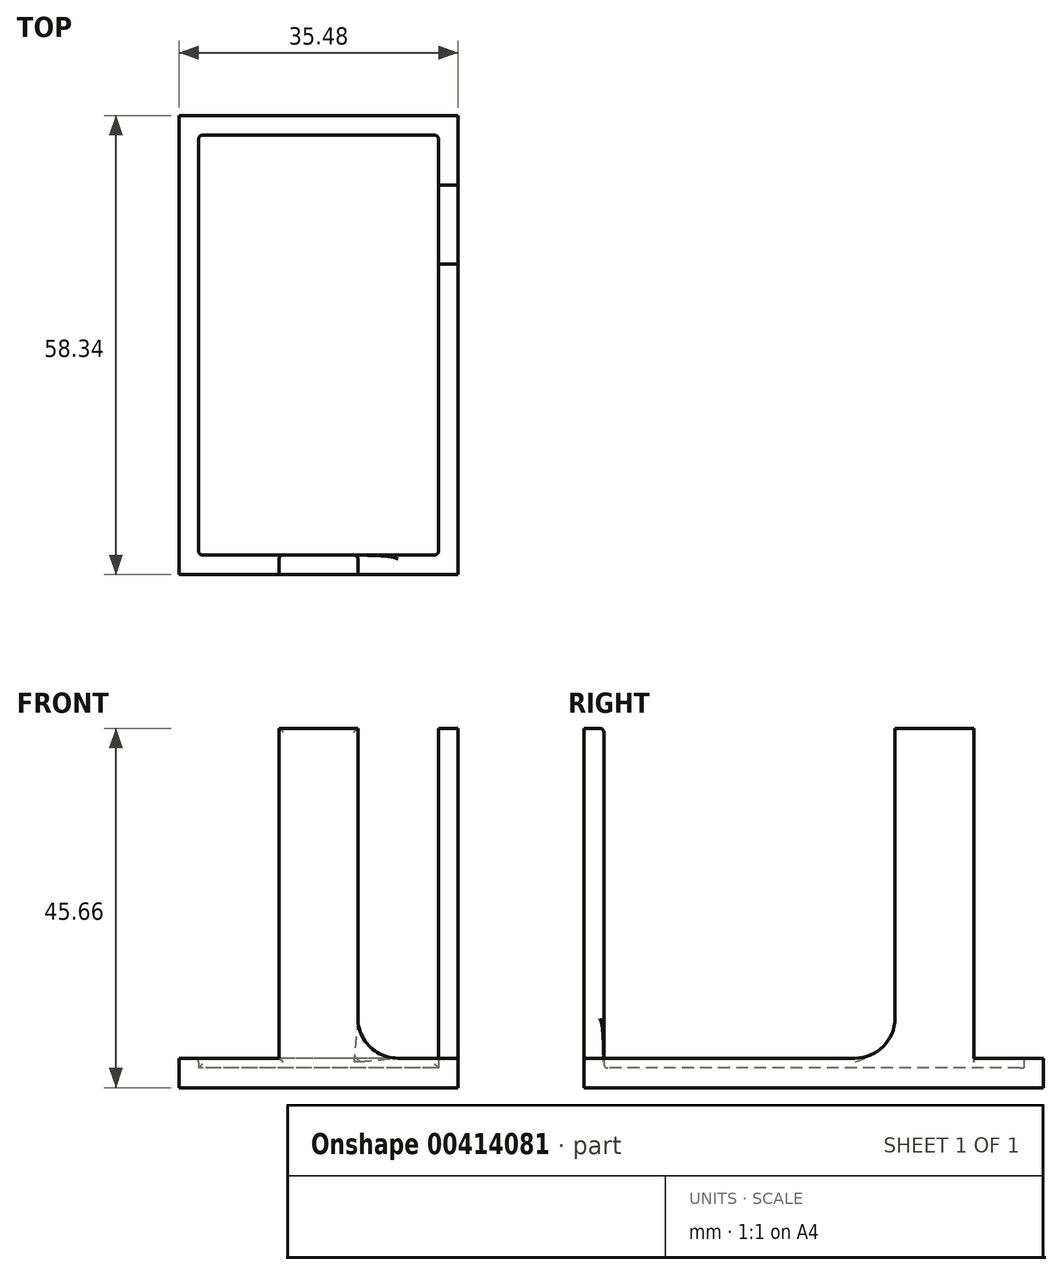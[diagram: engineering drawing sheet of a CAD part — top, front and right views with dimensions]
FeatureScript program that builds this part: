
annotation { "Feature Type Name" : "Feature", "Feature Type Description" : "" }
export const myFeature = defineFeature(function(context is Context, id is Id, definition is map)
    precondition{}
    {
        {
            var Q0;
            Q0=qCreatedBy(makeId("Top.planeOp"),FACE);
            var sketch = newSketch(context, id + "F0", { "sketchPlane" : qUnion([Q0])});
            skLineSegment(sketch, "E0.bottom", {"start": v(15.24, 26.67) * mm, "end": v(-15.24, 26.67) * mm});
            skLineSegment(sketch, "E0.top", {"start": v(15.24, -26.67) * mm, "end": v(-15.24, -26.67) * mm});
            skLineSegment(sketch, "E0.left", {"start": v(15.24, 26.67) * mm, "end": v(15.24, -26.67) * mm});
            skLineSegment(sketch, "E0.right", {"start": v(-15.24, 26.67) * mm, "end": v(-15.24, -26.67) * mm});
            skPoint(sketch, "E0.middle", {"position": v(0, 0) * mm});
            skSolve(sketch);
        }
        {
            var Q0;
            Q0=makeQuery(id+"F0.imprint","IMPRINT",FACE,{"disambiguationData":[TD([[makeQuery(id+"F0.imprint","IMPRINT",EDGE,{"derivedFrom":sQuery(id+"F0.wireOp",EDGE,"E0.bottom")}),1.0]])]});
            extrude(context, id + "F1", {"entities" : qUnion([Q0]), "depth" : 2.5 * mm});
        }
        {
            var Q0;
            Q0=makeQuery(id+"F1.opExtrude","SWEPT_FACE",FACE,{"disambiguationData":[OSD([sQuery(id+"F0.wireOp",EDGE,"E0.left")])]});
            var sketch = newSketch(context, id + "F2", { "sketchPlane" : qUnion([Q0])});
            skLineSegment(sketch, "E1.bottom", {"start": v(-26.67, 0) * mm, "end": v(26.67, 0) * mm});
            skLineSegment(sketch, "E1.top", {"start": v(-26.67, 1.25) * mm, "end": v(26.67, 1.25) * mm});
            skLineSegment(sketch, "E1.left", {"start": v(-26.67, 0) * mm, "end": v(-26.67, 1.25) * mm});
            skLineSegment(sketch, "E1.right", {"start": v(26.67, 0) * mm, "end": v(26.67, 1.25) * mm});
            skSolve(sketch);
        }
        {
            var Q0;
            Q0=makeQuery(id+"F1.opExtrude","SWEPT_FACE",FACE,{"disambiguationData":[OSD([sQuery(id+"F0.wireOp",EDGE,"E0.bottom")])]});
            var sketch = newSketch(context, id + "F3", { "sketchPlane" : qUnion([Q0])});
            skLineSegment(sketch, "E2.bottom", {"start": v(-15.24, 0) * mm, "end": v(15.24, 0) * mm});
            skLineSegment(sketch, "E2.top", {"start": v(-15.24, 1.25) * mm, "end": v(15.24, 1.25) * mm});
            skLineSegment(sketch, "E2.left", {"start": v(-15.24, 0) * mm, "end": v(-15.24, 1.25) * mm});
            skLineSegment(sketch, "E2.right", {"start": v(15.24, 0) * mm, "end": v(15.24, 1.25) * mm});
            skSolve(sketch);
        }
        {
            var Q0;
            Q0=makeQuery(id+"F1.opExtrude","SWEPT_FACE",FACE,{"disambiguationData":[OSD([sQuery(id+"F0.wireOp",EDGE,"E0.right")])]});
            var sketch = newSketch(context, id + "F4", { "sketchPlane" : qUnion([Q0])});
            skLineSegment(sketch, "E3.bottom", {"start": v(-26.67, 0) * mm, "end": v(26.67, 0) * mm});
            skLineSegment(sketch, "E3.top", {"start": v(-26.67, 1.25) * mm, "end": v(26.67, 1.25) * mm});
            skLineSegment(sketch, "E3.left", {"start": v(-26.67, 0) * mm, "end": v(-26.67, 1.25) * mm});
            skLineSegment(sketch, "E3.right", {"start": v(26.67, 0) * mm, "end": v(26.67, 1.25) * mm});
            skSolve(sketch);
        }
        {
            var Q0;
            Q0=makeQuery(id+"F1.opExtrude","SWEPT_FACE",FACE,{"disambiguationData":[OSD([sQuery(id+"F0.wireOp",EDGE,"E0.top")])]});
            var sketch = newSketch(context, id + "F5", { "sketchPlane" : qUnion([Q0])});
            skLineSegment(sketch, "E4.bottom", {"start": v(-15.24, 0) * mm, "end": v(15.24, 0) * mm});
            skLineSegment(sketch, "E4.top", {"start": v(-15.24, 1.25) * mm, "end": v(15.24, 1.25) * mm});
            skLineSegment(sketch, "E4.left", {"start": v(-15.24, 0) * mm, "end": v(-15.24, 1.25) * mm});
            skLineSegment(sketch, "E4.right", {"start": v(15.24, 0) * mm, "end": v(15.24, 1.25) * mm});
            skSolve(sketch);
        }
        {
            var Q0;
            Q0=makeQuery(id+"F2.imprint","IMPRINT",FACE,{"disambiguationData":[TD([[makeQuery(id+"F2.imprint","IMPRINT",EDGE,{"derivedFrom":sQuery(id+"F2.wireOp",EDGE,"E1.bottom")}),-1.0]])]});
            extrude(context, id + "F6", {"entities" : qUnion([Q0]), "operationType" : NewBodyOperationType.ADD, "depth" : 2.5 * mm});
        }
        {
            var Q0;
            Q0=makeQuery(id+"F5.imprint","IMPRINT",FACE,{"disambiguationData":[TD([[makeQuery(id+"F5.imprint","IMPRINT",EDGE,{"derivedFrom":sQuery(id+"F5.wireOp",EDGE,"E4.bottom")}),-1.0]])]});
            extrude(context, id + "F7", {"entities" : qUnion([Q0]), "operationType" : NewBodyOperationType.ADD, "depth" : 2.5 * mm});
        }
        {
            var Q0;
            Q0=makeQuery(id+"F7.opExtrude","SWEPT_FACE",FACE,{"disambiguationData":[OSD([sQuery(id+"F5.wireOp",EDGE,"E4.right")])]});
            extrude(context, id + "F8", {"entities" : qUnion([Q0]), "operationType" : NewBodyOperationType.ADD, "depth" : 2.5 * mm});
        }
        {
            var Q0;
            Q0=makeQuery(id+"F4.imprint","IMPRINT",FACE,{"disambiguationData":[TD([[makeQuery(id+"F4.imprint","IMPRINT",EDGE,{"derivedFrom":sQuery(id+"F4.wireOp",EDGE,"E3.bottom")}),1.0]])]});
            extrude(context, id + "F9", {"entities" : qUnion([Q0]), "operationType" : NewBodyOperationType.ADD, "depth" : 2.5 * mm});
        }
        {
            var Q0;
            Q0=makeQuery(id+"F9.opExtrude","SWEPT_FACE",FACE,{"disambiguationData":[OSD([sQuery(id+"F4.wireOp",EDGE,"E3.right")])]});
            extrude(context, id + "F10", {"entities" : qUnion([Q0]), "operationType" : NewBodyOperationType.ADD, "depth" : 2.5 * mm});
        }
        {
            var Q0;
            Q0=makeQuery(id+"F3.imprint","IMPRINT",FACE,{"disambiguationData":[TD([[makeQuery(id+"F3.imprint","IMPRINT",EDGE,{"derivedFrom":sQuery(id+"F3.wireOp",EDGE,"E2.bottom")}),1.0]])]});
            extrude(context, id + "F11", {"entities" : qUnion([Q0]), "operationType" : NewBodyOperationType.ADD, "depth" : 2.5 * mm});
        }
        {
            var Q0;
            Q0=makeQuery(id+"F11.opExtrude","SWEPT_FACE",FACE,{"disambiguationData":[OSD([sQuery(id+"F3.wireOp",EDGE,"E2.left")])]});
            extrude(context, id + "F12", {"entities" : qUnion([Q0]), "operationType" : NewBodyOperationType.ADD, "depth" : 2.5 * mm});
        }
        {
            var Q0;
            Q0=makeQuery(id+"F11.opExtrude","SWEPT_FACE",FACE,{"disambiguationData":[OSD([sQuery(id+"F3.wireOp",EDGE,"E2.right")])]});
            extrude(context, id + "F13", {"entities" : qUnion([Q0]), "operationType" : NewBodyOperationType.ADD, "depth" : 2.5 * mm});
        }
        {
            var Q0;
            {var subQ0=sQuery(id+"F3.wireOp",EDGE,"E2.top");var subQ1=sQuery(id+"F0.wireOp",EDGE,"E0.right");var subQ2=sQuery(id+"F0.wireOp",EDGE,"E0.bottom");var subQ3=sQuery(id+"F0.wireOp",EDGE,"E0.left");var subQ4=sQuery(id+"F4.wireOp",EDGE,"E3.top");var subQ5=sQuery(id+"F0.wireOp",EDGE,"E0.top");var subQ6=sQuery(id+"F5.wireOp",EDGE,"E4.top");Q0=makeQuery(id+"F13.boolean.opBoolean","MERGE",FACE,{"derivedFrom":[makeQuery(id+"F12.boolean.opBoolean","MERGE",FACE,{"derivedFrom":[makeQuery(id+"F10.boolean.opBoolean","MERGE",FACE,{"derivedFrom":[makeQuery(id+"F8.boolean.opBoolean","MERGE",FACE,{"derivedFrom":[makeQuery(id+"F6.opExtrude","SWEPT_FACE",FACE,{"disambiguationData":[OSD([sQuery(id+"F2.wireOp",EDGE,"E1.top")])]}),makeQuery(id+"F7.opExtrude","SWEPT_FACE",FACE,{"disambiguationData":[OSD([subQ6])]}),makeQuery(id+"F8.opExtrude","SWEPT_FACE",FACE,{"disambiguationData":[OSD([subQ5,subQ3,subQ6,sQuery(id+"F5.wireOp",EDGE,"E4.right")])]})]}),makeQuery(id+"F9.opExtrude","SWEPT_FACE",FACE,{"disambiguationData":[OSD([subQ4])]}),makeQuery(id+"F10.opExtrude","SWEPT_FACE",FACE,{"disambiguationData":[OSD([subQ5,subQ1,subQ4,sQuery(id+"F4.wireOp",EDGE,"E3.right")])]})]}),makeQuery(id+"F11.opExtrude","SWEPT_FACE",FACE,{"disambiguationData":[OSD([subQ0])]}),makeQuery(id+"F12.opExtrude","SWEPT_FACE",FACE,{"disambiguationData":[OSD([subQ2,subQ3,subQ0,sQuery(id+"F3.wireOp",EDGE,"E2.left")])]})]}),makeQuery(id+"F13.opExtrude","SWEPT_FACE",FACE,{"disambiguationData":[OSD([subQ2,subQ1,subQ0,sQuery(id+"F3.wireOp",EDGE,"E2.right")])]})]});}
            extrude(context, id + "F14", {"entities" : qUnion([Q0]), "operationType" : NewBodyOperationType.ADD, "depth" : 2.5 * mm});
        }
        {
            var Q0;
            Q0=makeQuery(id+"F14.opExtrude","CAP_FACE",FACE,{"disambiguationData":[OSD([sQuery(id+"F0.wireOp",EDGE,"E0.bottom"),sQuery(id+"F0.wireOp",EDGE,"E0.top"),sQuery(id+"F0.wireOp",EDGE,"E0.left"),sQuery(id+"F0.wireOp",EDGE,"E0.right"),sQuery(id+"F2.wireOp",EDGE,"E1.top"),sQuery(id+"F3.wireOp",EDGE,"E2.top"),sQuery(id+"F3.wireOp",EDGE,"E2.left"),sQuery(id+"F3.wireOp",EDGE,"E2.right"),sQuery(id+"F4.wireOp",EDGE,"E3.top"),sQuery(id+"F4.wireOp",EDGE,"E3.right"),sQuery(id+"F5.wireOp",EDGE,"E4.top"),sQuery(id+"F5.wireOp",EDGE,"E4.right")])],"isStart":false});
            var sketch = newSketch(context, id + "F15", { "sketchPlane" : qUnion([Q0])});
            skLineSegment(sketch, "E5.top", {"start": v(-15.24, -20.32) * mm, "end": v(-17.74, -20.32) * mm});
            skLineSegment(sketch, "E5.left", {"start": v(-15.24, -26.67) * mm, "end": v(-15.24, -20.32) * mm});
            skLineSegment(sketch, "E5.right", {"start": v(-17.74, -26.67) * mm, "end": v(-17.74, -20.32) * mm});
            skLineSegment(sketch, "E6.bottom", {"start": v(-17.74, -20.32) * mm, "end": v(-15.24, -20.32) * mm});
            skLineSegment(sketch, "E6.top", {"start": v(-17.74, -10.32) * mm, "end": v(-15.24, -10.32) * mm});
            skLineSegment(sketch, "E6.left", {"start": v(-17.74, -20.32) * mm, "end": v(-17.74, -10.32) * mm});
            skLineSegment(sketch, "E6.right", {"start": v(-15.24, -20.32) * mm, "end": v(-15.24, -10.32) * mm});
            skLineSegment(sketch, "E7.top", {"start": v(-15.24, 20.32) * mm, "end": v(-17.74, 20.32) * mm});
            skLineSegment(sketch, "E7.left", {"start": v(-15.24, 26.67) * mm, "end": v(-15.24, 20.32) * mm});
            skLineSegment(sketch, "E7.right", {"start": v(-17.74, 26.67) * mm, "end": v(-17.74, 20.32) * mm});
            skLineSegment(sketch, "E8.bottom", {"start": v(-17.74, 20.32) * mm, "end": v(-15.24, 20.32) * mm});
            skLineSegment(sketch, "E8.top", {"start": v(-17.74, 10.32) * mm, "end": v(-15.24, 10.32) * mm});
            skLineSegment(sketch, "E8.left", {"start": v(-17.74, 20.32) * mm, "end": v(-17.74, 10.32) * mm});
            skLineSegment(sketch, "E8.right", {"start": v(-15.24, 20.32) * mm, "end": v(-15.24, 10.32) * mm});
            skLineSegment(sketch, "E9.top", {"start": v(15.24, 20.32) * mm, "end": v(17.74, 20.32) * mm});
            skLineSegment(sketch, "E9.left", {"start": v(15.24, 26.67) * mm, "end": v(15.24, 20.32) * mm});
            skLineSegment(sketch, "E9.right", {"start": v(17.74, 26.67) * mm, "end": v(17.74, 20.32) * mm});
            skLineSegment(sketch, "E10.bottom", {"start": v(15.24, 10.32) * mm, "end": v(17.74, 10.32) * mm});
            skLineSegment(sketch, "E10.left", {"start": v(15.24, 10.32) * mm, "end": v(15.24, 20.32) * mm});
            skLineSegment(sketch, "E10.right", {"start": v(17.74, 10.32) * mm, "end": v(17.74, 20.32) * mm});
            skLineSegment(sketch, "E11.top", {"start": v(15.24, -20.32) * mm, "end": v(17.74, -20.32) * mm});
            skLineSegment(sketch, "E11.left", {"start": v(15.24, -26.67) * mm, "end": v(15.24, -20.32) * mm});
            skLineSegment(sketch, "E11.right", {"start": v(17.74, -26.67) * mm, "end": v(17.74, -20.32) * mm});
            skLineSegment(sketch, "E12.bottom", {"start": v(17.74, -20.32) * mm, "end": v(15.24, -20.32) * mm});
            skLineSegment(sketch, "E12.top", {"start": v(17.74, -10.32) * mm, "end": v(15.24, -10.32) * mm});
            skLineSegment(sketch, "E12.left", {"start": v(17.74, -20.32) * mm, "end": v(17.74, -10.32) * mm});
            skLineSegment(sketch, "E12.right", {"start": v(15.24, -20.32) * mm, "end": v(15.24, -10.32) * mm});
            skPoint(sketch, "E13.middle", {"position": v(0, 27.92) * mm});
            skLineSegment(sketch, "E14", {"start": v(0, -27.92) * mm, "end": v(0, -29.17) * mm});
            skLineSegment(sketch, "E15.bottom", {"start": v(-5, -26.67) * mm, "end": v(5, -26.67) * mm});
            skLineSegment(sketch, "E15.top", {"start": v(-5, -29.17) * mm, "end": v(5, -29.17) * mm});
            skLineSegment(sketch, "E15.left", {"start": v(-5, -26.67) * mm, "end": v(-5, -29.17) * mm});
            skLineSegment(sketch, "E15.right", {"start": v(5, -26.67) * mm, "end": v(5, -29.17) * mm});
            skPoint(sketch, "E15.middle", {"position": v(0, -27.92) * mm});
            skPoint(sketch, "E16.orphan", {"position": v(0, -26.67) * mm});
            skPoint(sketch, "E17.orphan", {"position": v(0, 29.17) * mm});
            skPoint(sketch, "E18.start.orphan", {"position": v(0, 26.67) * mm});
            skPoint(sketch, "E19.orphan", {"position": v(5, 26.67) * mm});
            skPoint(sketch, "E13.left.start.orphan", {"position": v(-5, 26.67) * mm});
            skPoint(sketch, "E20.orphan", {"position": v(-5, 29.17) * mm});
            skPoint(sketch, "E13.top.end.orphan", {"position": v(5, 29.17) * mm});
            skSolve(sketch);
        }
        {
            var Q0;
            Q0=makeQuery(id+"F15.imprint","IMPRINT",FACE,{"disambiguationData":[TD([[makeQuery(id+"F15.imprint","IMPRINT",EDGE,{"derivedFrom":sQuery(id+"F15.wireOp",EDGE,"E6.bottom")}),1.0]])]});
            var Q1;
            Q1=makeQuery(id+"F15.imprint","IMPRINT",FACE,{"disambiguationData":[TD([[makeQuery(id+"F15.imprint","IMPRINT",EDGE,{"derivedFrom":sQuery(id+"F15.wireOp",EDGE,"E8.bottom")}),-1.0]])]});
            var Q2;
            Q2=makeQuery(id+"F15.imprint","IMPRINT",FACE,{"disambiguationData":[TD([[makeQuery(id+"F15.imprint","IMPRINT",EDGE,{"derivedFrom":sQuery(id+"F15.wireOp",EDGE,"E13.top")}),1.0]])]});
            var Q3;
            Q3=makeQuery(id+"F15.imprint","IMPRINT",FACE,{"disambiguationData":[TD([[makeQuery(id+"F15.imprint","IMPRINT",EDGE,{"derivedFrom":sQuery(id+"F15.wireOp",EDGE,"E10.bottom")}),1.0]])]});
            var Q4;
            Q4=makeQuery(id+"F15.imprint","IMPRINT",FACE,{"disambiguationData":[TD([[makeQuery(id+"F15.imprint","IMPRINT",EDGE,{"derivedFrom":sQuery(id+"F15.wireOp",EDGE,"E12.bottom")}),-1.0]])]});
            var Q5;
            Q5=makeQuery(id+"F15.imprint","IMPRINT",FACE,{"disambiguationData":[TD([[makeQuery(id+"F15.imprint","IMPRINT",EDGE,{"derivedFrom":sQuery(id+"F15.wireOp",EDGE,"E15.bottom")}),-1.0]])]});
            extrude(context, id + "F16", {"entities" : qUnion([Q0, Q1, Q2, Q3, Q4, Q5]), "operationType" : NewBodyOperationType.ADD, "depth" : 41.9 * mm});
        }
        {
            var Q0;
            Q0=makeQuery(id+"F1.opExtrude","CAP_EDGE",EDGE,{"disambiguationData":[OSD([sQuery(id+"F0.wireOp",EDGE,"E0.right")])],"isStart":false});
            var Q1;
            Q1=makeQuery(id+"F14.opExtrude","SWEPT_EDGE",EDGE,{"disambiguationData":[OSD([sQuery(id+"F0.wireOp",EDGE,"E0.bottom"),sQuery(id+"F0.wireOp",EDGE,"E0.right"),sQuery(id+"F3.wireOp",EDGE,"E2.top"),sQuery(id+"F3.wireOp",EDGE,"E2.right"),sQuery(id+"F4.wireOp",EDGE,"E3.top"),sQuery(id+"F4.wireOp",EDGE,"E3.left")])]});
            var Q2;
            Q2=makeQuery(id+"F1.opExtrude","CAP_EDGE",EDGE,{"disambiguationData":[OSD([sQuery(id+"F0.wireOp",EDGE,"E0.bottom")])],"isStart":false});
            var Q3;
            Q3=makeQuery(id+"F14.opExtrude","SWEPT_EDGE",EDGE,{"disambiguationData":[OSD([sQuery(id+"F0.wireOp",EDGE,"E0.bottom"),sQuery(id+"F0.wireOp",EDGE,"E0.left"),sQuery(id+"F2.wireOp",EDGE,"E1.top"),sQuery(id+"F2.wireOp",EDGE,"E1.right"),sQuery(id+"F3.wireOp",EDGE,"E2.top"),sQuery(id+"F3.wireOp",EDGE,"E2.left")])]});
            var Q4;
            Q4=makeQuery(id+"F14.opExtrude","SWEPT_EDGE",EDGE,{"disambiguationData":[OSD([sQuery(id+"F0.wireOp",EDGE,"E0.top"),sQuery(id+"F0.wireOp",EDGE,"E0.left"),sQuery(id+"F2.wireOp",EDGE,"E1.top"),sQuery(id+"F2.wireOp",EDGE,"E1.left"),sQuery(id+"F5.wireOp",EDGE,"E4.top"),sQuery(id+"F5.wireOp",EDGE,"E4.right")])]});
            var Q5;
            Q5=makeQuery(id+"F1.opExtrude","CAP_EDGE",EDGE,{"disambiguationData":[OSD([sQuery(id+"F0.wireOp",EDGE,"E0.left")])],"isStart":false});
            var Q6;
            Q6=makeQuery(id+"F14.opExtrude","SWEPT_EDGE",EDGE,{"disambiguationData":[OSD([sQuery(id+"F0.wireOp",EDGE,"E0.top"),sQuery(id+"F0.wireOp",EDGE,"E0.right"),sQuery(id+"F4.wireOp",EDGE,"E3.top"),sQuery(id+"F4.wireOp",EDGE,"E3.right"),sQuery(id+"F5.wireOp",EDGE,"E4.top"),sQuery(id+"F5.wireOp",EDGE,"E4.left")])]});
            var Q7;
            Q7=makeQuery(id+"F16.boolean.opBoolean","MERGE",FACE,{"derivedFrom":[makeQuery(id+"F14.opExtrude","SWEPT_FACE",FACE,{"disambiguationData":[OSD([sQuery(id+"F5.wireOp",EDGE,"E4.top")])]}),makeQuery(id+"F16.opExtrude","SWEPT_FACE",FACE,{"disambiguationData":[OSD([sQuery(id+"F15.wireOp",EDGE,"E15.bottom")])]})]});
            var Q8;
            {var subQ0=sQuery(id+"F4.wireOp",EDGE,"E3.top");Q8=makeQuery(id+"F16.boolean.opBoolean","SPLIT",EDGE,{"disambiguationData":[TD([makeQuery(id+"F16.opExtrude","SWEPT_FACE",FACE,{"disambiguationData":[OSD([sQuery(id+"F15.wireOp",EDGE,"E6.top")])]})])],"derivedFrom":makeQuery(id+"F14.opExtrude","CAP_EDGE",EDGE,{"disambiguationData":[OSD([subQ0])],"isStart":false})});}
            var Q9;
            {var subQ0=sQuery(id+"F4.wireOp",EDGE,"E3.top");var subQ1=sQuery(id+"F3.wireOp",EDGE,"E2.top");Q9=makeQuery(id+"F16.boolean.opBoolean","SPLIT",EDGE,{"disambiguationData":[TD([makeQuery(id+"F14.opExtrude","SWEPT_FACE",FACE,{"disambiguationData":[OSD([subQ0])]})])],"derivedFrom":makeQuery(id+"F14.opExtrude","CAP_EDGE",EDGE,{"disambiguationData":[OSD([subQ1])],"isStart":false})});}
            var Q10;
            {var subQ0=sQuery(id+"F3.wireOp",EDGE,"E2.top");var subQ1=sQuery(id+"F2.wireOp",EDGE,"E1.top");Q10=makeQuery(id+"F16.boolean.opBoolean","SPLIT",EDGE,{"disambiguationData":[TD([makeQuery(id+"F14.opExtrude","SWEPT_FACE",FACE,{"disambiguationData":[OSD([subQ1])]})])],"derivedFrom":makeQuery(id+"F14.opExtrude","CAP_EDGE",EDGE,{"disambiguationData":[OSD([subQ0])],"isStart":false})});}
            var Q11;
            {var subQ0=sQuery(id+"F3.wireOp",EDGE,"E2.top");var subQ1=sQuery(id+"F2.wireOp",EDGE,"E1.top");Q11=makeQuery(id+"F16.boolean.opBoolean","SPLIT",EDGE,{"disambiguationData":[TD([makeQuery(id+"F14.opExtrude","SWEPT_FACE",FACE,{"disambiguationData":[OSD([subQ0])]})])],"derivedFrom":makeQuery(id+"F14.opExtrude","CAP_EDGE",EDGE,{"disambiguationData":[OSD([subQ1])],"isStart":false})});}
            var Q12;
            {var subQ0=sQuery(id+"F2.wireOp",EDGE,"E1.top");Q12=makeQuery(id+"F16.boolean.opBoolean","SPLIT",EDGE,{"disambiguationData":[TD([makeQuery(id+"F16.opExtrude","SWEPT_FACE",FACE,{"disambiguationData":[OSD([sQuery(id+"F15.wireOp",EDGE,"E10.bottom")])]})])],"derivedFrom":makeQuery(id+"F14.opExtrude","CAP_EDGE",EDGE,{"disambiguationData":[OSD([subQ0])],"isStart":false})});}
            fillet(context, id + "F17", {"entities" : qUnion([Q0, Q1, Q2, Q3, Q4, Q5, Q6, Q7, Q8, Q9, Q10, Q11, Q12]), "radius" : 0.5 * mm, "tangentPropagation" : true, "allowEdgeOverflow" : false});
        }
        {
            var Q0;
            Q0=makeQuery(id+"F16.opExtrude","CAP_EDGE",EDGE,{"disambiguationData":[OSD([sQuery(id+"F15.wireOp",EDGE,"E9.top")])],"isStart":true});
            var Q1;
            Q1=makeQuery(id+"F16.opExtrude","CAP_EDGE",EDGE,{"disambiguationData":[OSD([sQuery(id+"F15.wireOp",EDGE,"E10.bottom")])],"isStart":true});
            var Q2;
            Q2=makeQuery(id+"F16.opExtrude","CAP_EDGE",EDGE,{"disambiguationData":[OSD([sQuery(id+"F15.wireOp",EDGE,"E12.top")])],"isStart":true});
            var Q3;
            Q3=makeQuery(id+"F16.opExtrude","CAP_EDGE",EDGE,{"disambiguationData":[OSD([sQuery(id+"F15.wireOp",EDGE,"E12.bottom")])],"isStart":true});
            var Q4;
            Q4=makeQuery(id+"F16.opExtrude","CAP_EDGE",EDGE,{"disambiguationData":[OSD([sQuery(id+"F15.wireOp",EDGE,"E15.right")])],"isStart":true});
            var Q5;
            Q5=makeQuery(id+"F16.opExtrude","CAP_EDGE",EDGE,{"disambiguationData":[OSD([sQuery(id+"F15.wireOp",EDGE,"E15.left")])],"isStart":true});
            var Q6;
            Q6=makeQuery(id+"F16.opExtrude","CAP_EDGE",EDGE,{"disambiguationData":[OSD([sQuery(id+"F15.wireOp",EDGE,"E6.bottom")])],"isStart":true});
            var Q7;
            Q7=makeQuery(id+"F16.opExtrude","CAP_EDGE",EDGE,{"disambiguationData":[OSD([sQuery(id+"F15.wireOp",EDGE,"E6.top")])],"isStart":true});
            var Q8;
            Q8=makeQuery(id+"F16.opExtrude","CAP_EDGE",EDGE,{"disambiguationData":[OSD([sQuery(id+"F15.wireOp",EDGE,"E8.top")])],"isStart":true});
            var Q9;
            Q9=makeQuery(id+"F16.opExtrude","CAP_EDGE",EDGE,{"disambiguationData":[OSD([sQuery(id+"F15.wireOp",EDGE,"E8.bottom")])],"isStart":true});
            fillet(context, id + "F18", {"entities" : qUnion([Q0, Q1, Q2, Q3, Q4, Q5, Q6, Q7, Q8, Q9]), "radius" : 5.08 * mm, "tangentPropagation" : true, "allowEdgeOverflow" : false});
        }
    });
